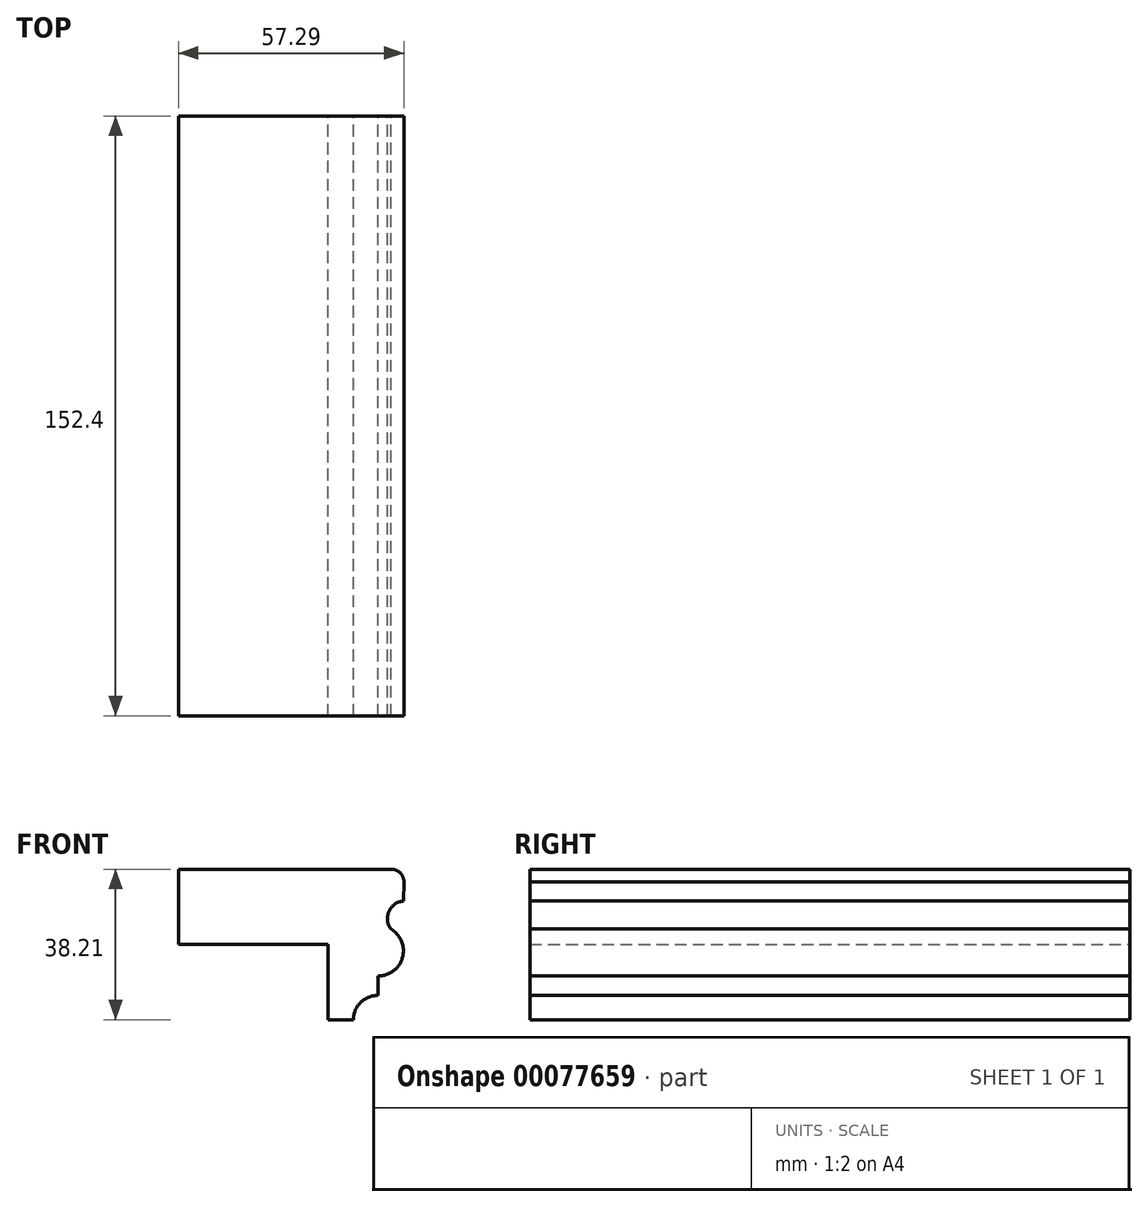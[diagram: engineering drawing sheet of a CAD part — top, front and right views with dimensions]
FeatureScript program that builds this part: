
annotation { "Feature Type Name" : "Feature", "Feature Type Description" : "" }
export const myFeature = defineFeature(function(context is Context, id is Id, definition is map)
    precondition{}
    {
        {
            var Q0;
            Q0=qCreatedBy(makeId("Front.planeOp"),FACE);
            var sketch = newSketch(context, id + "F0", { "sketchPlane" : qUnion([Q0])});
            skLineSegment(sketch, "E0", {"start": v(-28.6, 0) * mm, "end": v(-28.6, 19.14) * mm});
            skLineSegment(sketch, "E1", {"start": v(-28.6, 19.14) * mm, "end": v(9.46, 19.14) * mm});
            skLineSegment(sketch, "E2", {"start": v(9.46, 19.14) * mm, "end": v(9.46, 0) * mm});
            skLineSegment(sketch, "E3", {"start": v(9.46, 0) * mm, "end": v(-28.6, 0) * mm});
            skLineSegment(sketch, "E4", {"start": v(9.46, 19.14) * mm, "end": v(25.5, 19.14) * mm});
            skLineSegment(sketch, "E5", {"start": v(9.46, 19.14) * mm, "end": v(9.46, -19.07) * mm});
            skLineSegment(sketch, "E6", {"start": v(9.46, -19.07) * mm, "end": v(15.85, -19.07) * mm});
            skArc(sketch, "E7", {"start": v(15.85, -19.07) * mm, "mid": v(17.71, -14.67) * mm, "end": v(22.16, -12.93) * mm});
            skLineSegment(sketch, "E8", {"start": v(22.16, -12.93) * mm, "end": v(22.16, -7.96) * mm});
            skArc(sketch, "E9", {"start": v(28.56, -1.58) * mm, "mid": v(26.68, -6.1) * mm, "end": v(22.16, -7.98) * mm});
            skArc(sketch, "E10", {"start": v(25.38, 3.94) * mm, "mid": v(27.7, 1.6) * mm, "end": v(28.56, -1.58) * mm});
            skArc(sketch, "E11", {"start": v(25.38, 3.94) * mm, "mid": v(24.9, 8.43) * mm, "end": v(28.56, 11.06) * mm});
            skArc(sketch, "E12", {"start": v(25.5, 19.14) * mm, "mid": v(27.77, 18.18) * mm, "end": v(28.7, 15.89) * mm});
            skLineSegment(sketch, "E13", {"start": v(28.7, 15.89) * mm, "end": v(28.56, 11.06) * mm});
            skSolve(sketch);
        }
        {
            var Q0;
            Q0=makeQuery(id+"F0.imprint","IMPRINT",FACE,{"disambiguationData":[TD([[makeQuery(id+"F0.imprint","IMPRINT",EDGE,{"derivedFrom":sQuery(id+"F0.wireOp",EDGE,"E0")}),-1.0]])]});
            var Q1;
            {var subQ3=sQuery(id+"F0.wireOp",EDGE,"E4");Q1=makeQuery(id+"F0.imprint","IMPRINT",FACE,{"disambiguationData":[TD([[makeQuery(id+"F0.imprint","IMPRINT",EDGE,{"derivedFrom":subQ3}),-1.0]])]});}
            extrude(context, id + "F1", {"entities" : qUnion([Q0, Q1]), "depth" : 152.4 * mm});
        }
    });
